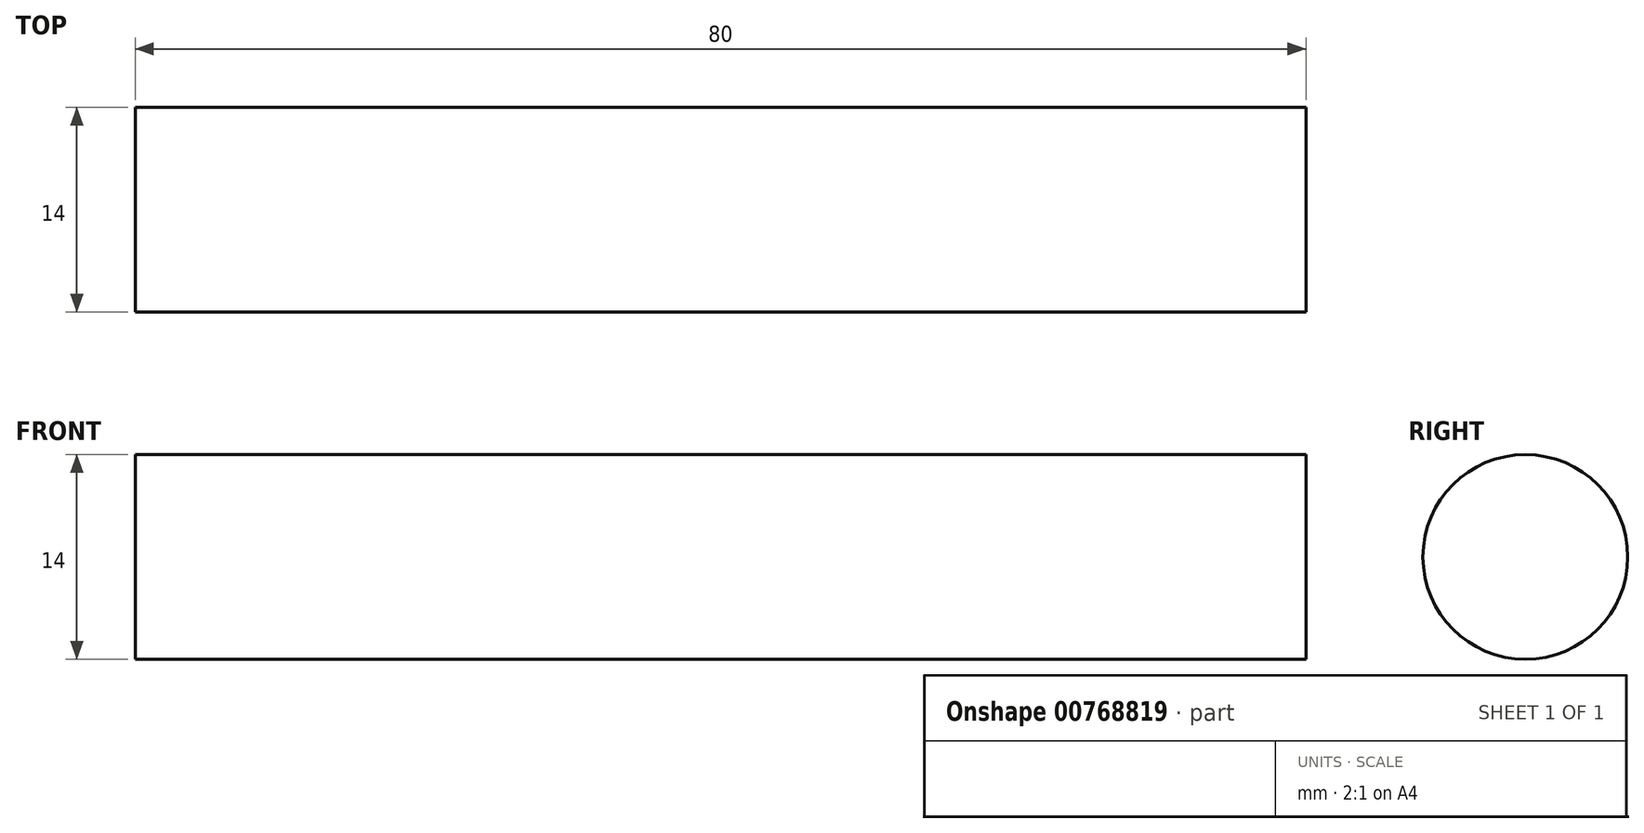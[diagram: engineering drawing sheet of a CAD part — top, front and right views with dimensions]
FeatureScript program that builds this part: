
annotation { "Feature Type Name" : "Feature", "Feature Type Description" : "" }
export const myFeature = defineFeature(function(context is Context, id is Id, definition is map)
    precondition{}
    {
        {
            var Q0;
            Q0=qCreatedBy(makeId("Right.planeOp"),FACE);
            var sketch = newSketch(context, id + "F0", { "sketchPlane" : qUnion([Q0])});
            skCircle(sketch, "E0", {"center": v(0, 0) * mm, "radius": 7 * mm});
            skSolve(sketch);
        }
        {
            var Q0;
            Q0=makeQuery(id+"F0.imprint","IMPRINT",FACE,{"disambiguationData":[TD([[makeQuery(id+"F0.imprint","IMPRINT",EDGE,{"derivedFrom":sQuery(id+"F0.wireOp",EDGE,"E0")}),1.0]])]});
            extrude(context, id + "F1", {"entities" : qUnion([Q0]), "endBound" : BoundingType.SYMMETRIC, "depth" : 80 * mm, "offsetDistance" : 25 * mm});
        }
        {
            var Q0;
            Q0=qCreatedBy(makeId("Top.planeOp"),FACE);
            var sketch = newSketch(context, id + "F2", { "sketchPlane" : qUnion([Q0])});
            skCircle(sketch, "E1", {"center": v(0, 0) * mm, "radius": 7 * mm});
            skSolve(sketch);
        }
        {
            var Q0;
            Q0=sQuery(id+"F2.wireOp",EDGE,"E1");
            extrude(context, id + "F3", {"bodyType" : ToolBodyType.SURFACE, "surfaceEntities" : qUnion([Q0]), "oppositeDirection" : true, "depth" : 50 * mm, "offsetDistance" : 25 * mm});
        }
        {
            var Q0;
            Q0=qCreatedBy(makeId("Top.planeOp"),FACE);
            cPlane(context, id + "F4", {"entities" : qUnion([Q0]), "cplaneType" : CPlaneType.OFFSET, "offset" : 50 * mm, "oppositeDirection" : true, "width" : 150 * mm, "height" : 150 * mm});
        }
        {
            var Q0;
            Q0=qCreatedBy(id+"F4.planeOp",FACE);
            var sketch = newSketch(context, id + "F5", { "sketchPlane" : qUnion([Q0])});
            skCircle(sketch, "E2", {"center": v(0, 0) * mm, "radius": 8 * mm});
            skSolve(sketch);
        }
        {
            var Q0;
            Q0=sQuery(id+"F5.wireOp",EDGE,"E2");
            extrude(context, id + "F6", {"bodyType" : ToolBodyType.SURFACE, "surfaceEntities" : qUnion([Q0]), "oppositeDirection" : true, "depth" : 100 * mm, "offsetDistance" : 25 * mm});
        }
    });
